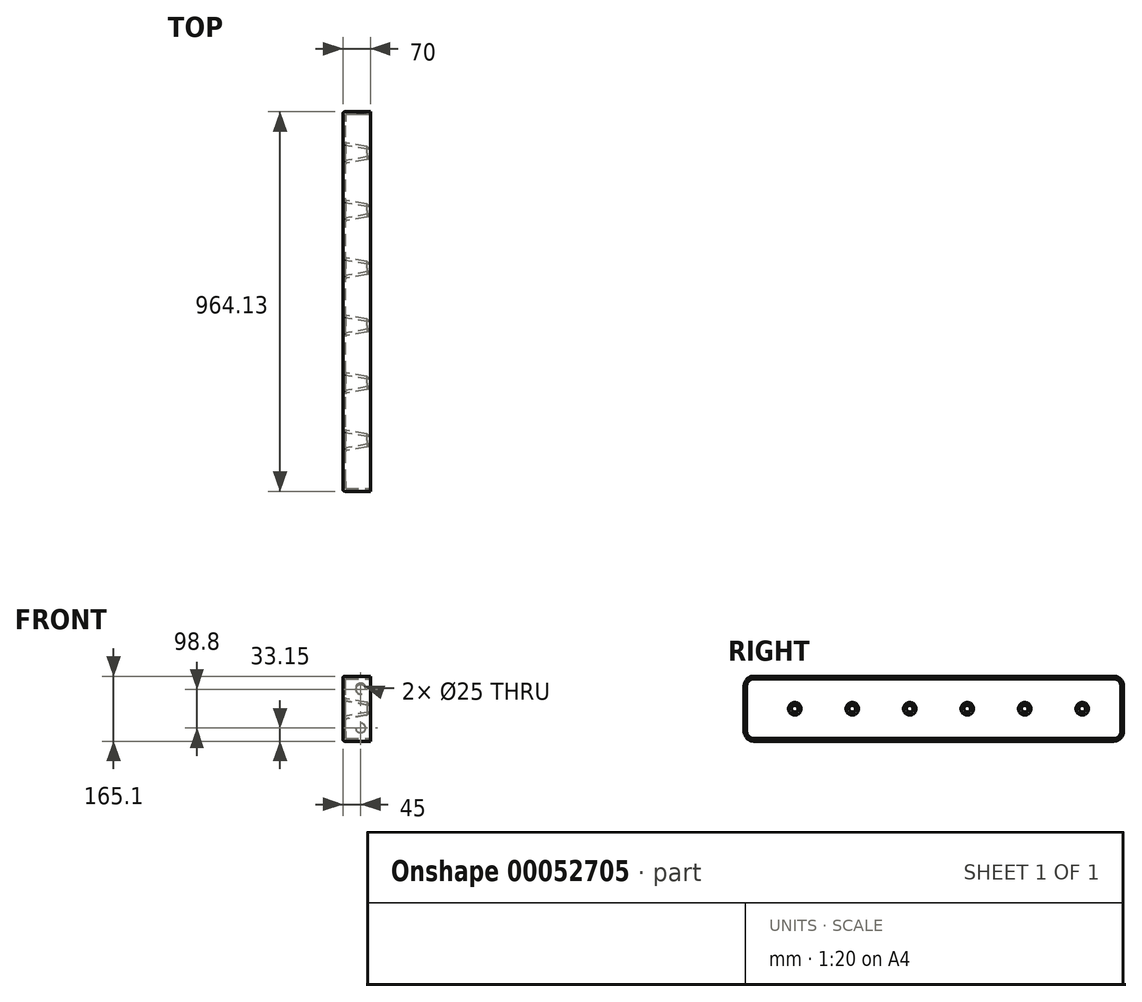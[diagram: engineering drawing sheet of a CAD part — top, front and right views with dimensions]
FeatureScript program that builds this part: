
annotation { "Feature Type Name" : "Feature", "Feature Type Description" : "" }
export const myFeature = defineFeature(function(context is Context, id is Id, definition is map)
    precondition{}
    {
        {
            var Q0;
            Q0=qCreatedBy(makeId("Right.planeOp"),FACE);
            var sketch = newSketch(context, id + "F0", { "sketchPlane" : qUnion([Q0])});
            skLineSegment(sketch, "E0.rect.bottom", {"start": v(-457.5, 82.55) * mm, "end": v(457.5, 82.55) * mm});
            skLineSegment(sketch, "E0.rect.top", {"start": v(-457.5, -82.55) * mm, "end": v(457.5, -82.55) * mm});
            skLineSegment(sketch, "E0.rect.left", {"start": v(-457.5, 82.55) * mm, "end": v(-457.5, -82.55) * mm});
            skLineSegment(sketch, "E0.rect.right", {"start": v(457.5, 82.55) * mm, "end": v(457.5, -82.55) * mm});
            skPoint(sketch, "E0.rect.middle", {"position": v(0, 0) * mm});
            skLineSegment(sketch, "E1.0", {"start": v(-447.34, 72.39) * mm, "end": v(447.34, 72.39) * mm, "construction": true});
            skLineSegment(sketch, "E1.1", {"start": v(-447.34, 72.39) * mm, "end": v(-447.34, -72.39) * mm, "construction": true});
            skLineSegment(sketch, "E1.2", {"start": v(-447.34, -72.39) * mm, "end": v(447.34, -72.39) * mm, "construction": true});
            skLineSegment(sketch, "E1.3", {"start": v(447.34, 72.39) * mm, "end": v(447.34, -72.39) * mm, "construction": true});
            skLineSegment(sketch, "E2", {"start": v(-457.5, 82.55) * mm, "end": v(457.5, -82.55) * mm, "construction": true});
            skLineSegment(sketch, "E3", {"start": v(457.5, 82.55) * mm, "end": v(-457.5, -82.55) * mm, "construction": true});
            skSolve(sketch);
        }
        {
            var Q0;
            Q0=makeQuery(id+"F0.imprint","IMPRINT",FACE,{"disambiguationData":[TD([[makeQuery(id+"F0.imprint","IMPRINT",EDGE,{"derivedFrom":sQuery(id+"F0.wireOp",EDGE,"E0.rect.bottom")}),-1.0]])]});
            extrude(context, id + "F1", {"entities" : qUnion([Q0]), "depth" : 70 * mm});
        }
        {
            var Q0;
            Q0=makeQuery(id+"F1.opExtrude","SWEPT_FACE",FACE,{"disambiguationData":[OSD([sQuery(id+"F0.wireOp",EDGE,"E0.rect.left")])]});
            extrude(context, id + "F2", {"entities" : qUnion([Q0]), "operationType" : NewBodyOperationType.ADD, "depth" : 36.63 * mm});
        }
        {
            var Q0;
            Q0=makeQuery(id+"F1.opExtrude","SWEPT_FACE",FACE,{"disambiguationData":[OSD([sQuery(id+"F0.wireOp",EDGE,"E0.rect.right")])]});
            extrude(context, id + "F3", {"entities" : qUnion([Q0]), "operationType" : NewBodyOperationType.ADD, "depth" : 12.5 * mm});
        }
        {
            var Q0;
            Q0=makeQuery(id+"F0.imprint","IMPRINT",FACE,{"disambiguationData":[TD([[makeQuery(id+"F0.imprint","IMPRINT",EDGE,{"derivedFrom":sQuery(id+"F0.wireOp",EDGE,"E0.rect.bottom")}),-1.0]])]});
            var sketch = newSketch(context, id + "F4", { "sketchPlane" : qUnion([Q0])});
            skLineSegment(sketch, "E4", {"start": v(-457.5, 0) * mm, "end": v(457.5, 0) * mm, "construction": true});
            skCircle(sketch, "E5", {"center": v(-365.13, 0) * mm, "radius": 20.32 * mm});
            skCircle(sketch, "E6", {"center": v(-73.03, 0) * mm, "radius": 20.32 * mm});
            skCircle(sketch, "E7.MirrorC", {"center": v(73.03, 0) * mm, "radius": 20.32 * mm});
            skCircle(sketch, "E8", {"center": v(-219.08, 0) * mm, "radius": 20.32 * mm});
            skCircle(sketch, "E9", {"center": v(219.08, 0) * mm, "radius": 20.32 * mm});
            skCircle(sketch, "E10", {"center": v(365.13, 0) * mm, "radius": 20.32 * mm});
            skSolve(sketch);
        }
        {
            var Q0;
            Q0 = qSketchRegion(id + "F4", true);
            extrude(context, id + "F5", {"entities" : qUnion([Q0]), "operationType" : NewBodyOperationType.REMOVE, "endBound" : BoundingType.THROUGH_ALL, "depth" : 25 * mm, "hasDraft" : true, "draftAngle" : 10 * degree, "draftPullDirection" : true});
        }
        {
            var Q0;
            {var subQ0=makeQuery(id+"FMJtkyeOeprAO9Q_1.hole-4.opRevolve","SWEPT_FACE",FACE,{"disambiguationData":[OSD([sQuery(id+"FMJtkyeOeprAO9Q_1.hole-4.sketch.wireOp",EDGE,"cbore_start_line_2")])]});var subQ1=makeQuery(id+"FMJtkyeOeprAO9Q_1.hole-2.boolean.opBoolean","COPY",FACE,{"derivedFrom":makeQuery(id+"FMJtkyeOeprAO9Q_1.hole-2.opRevolve","SWEPT_FACE",FACE,{"disambiguationData":[OSD([sQuery(id+"FMJtkyeOeprAO9Q_1.hole-2.sketch.wireOp",EDGE,"cbore_start_line_2")])]})});var subQ2=sQuery(id+"F0.wireOp",EDGE,"E0.rect.top");var subQ3=makeQuery(id+"F1.opExtrude","SWEPT_FACE",FACE,{"disambiguationData":[OSD([subQ2])]});var subQ4=makeQuery(id+"FMJtkyeOeprAO9Q_1.hole-3.opRevolve","SWEPT_FACE",FACE,{"disambiguationData":[OSD([sQuery(id+"FMJtkyeOeprAO9Q_1.hole-3.sketch.wireOp",EDGE,"cbore_start_line_2")])]});var subQ5=makeQuery(id+"FMJtkyeOeprAO9Q_1.hole-3.boolean.opBoolean","COPY",FACE,{"disambiguationData":[OD(1.0)],"derivedFrom":subQ4});var subQ6=makeQuery(id+"FMJtkyeOeprAO9Q_1.hole-0.opRevolve","SWEPT_FACE",FACE,{"disambiguationData":[OSD([sQuery(id+"FMJtkyeOeprAO9Q_1.hole-0.sketch.wireOp",EDGE,"cbore_start_line_2")])]});var subQ7=makeQuery(id+"FMJtkyeOeprAO9Q_1.hole-0.boolean.opBoolean","COPY",FACE,{"disambiguationData":[OD(1.0)],"derivedFrom":subQ6});var subQ8=makeQuery(id+"FMJtkyeOeprAO9Q_1.hole-1.boolean.opBoolean","COPY",FACE,{"derivedFrom":makeQuery(id+"FMJtkyeOeprAO9Q_1.hole-1.opRevolve","SWEPT_FACE",FACE,{"disambiguationData":[OSD([sQuery(id+"FMJtkyeOeprAO9Q_1.hole-1.sketch.wireOp",EDGE,"cbore_start_line_2")])]})});var subQ9=sQuery(id+"F0.wireOp",EDGE,"E0.rect.bottom");var subQ10=makeQuery(id+"F1.opExtrude","SWEPT_FACE",FACE,{"disambiguationData":[OSD([subQ9])]});var subQ11=sQuery(id+"F0.wireOp",EDGE,"E0.rect.left");var subQ12=makeQuery(id+"F1.opExtrude","SWEPT_FACE",FACE,{"disambiguationData":[OSD([subQ11])]});var subQ13=sQuery(id+"F0.wireOp",EDGE,"E0.rect.right");var subQ14=makeQuery(id+"F1.opExtrude","SWEPT_FACE",FACE,{"disambiguationData":[OSD([subQ13])]});Q0=makeQuery(id+"FMJtkyeOeprAO9Q_1.hole-7.boolean.opBoolean","SPLIT",FACE,{"disambiguationData":[TD([subQ10,subQ3,subQ12,subQ14,subQ7,subQ8,subQ1,subQ5,makeQuery(id+"FMJtkyeOeprAO9Q_1.hole-4.boolean.opBoolean","COPY",FACE,{"disambiguationData":[OD(1.0)],"derivedFrom":subQ0}),makeQuery(id+"FMJtkyeOeprAO9Q_1.hole-5.boolean.opBoolean","COPY",FACE,{"derivedFrom":makeQuery(id+"FMJtkyeOeprAO9Q_1.hole-5.opRevolve","SWEPT_FACE",FACE,{"disambiguationData":[OSD([sQuery(id+"FMJtkyeOeprAO9Q_1.hole-5.sketch.wireOp",EDGE,"cbore_start_line_2")])]})}),makeQuery(id+"FMJtkyeOeprAO9Q_1.hole-6.boolean.opBoolean","COPY",FACE,{"derivedFrom":makeQuery(id+"FMJtkyeOeprAO9Q_1.hole-6.opRevolve","SWEPT_FACE",FACE,{"disambiguationData":[OSD([sQuery(id+"FMJtkyeOeprAO9Q_1.hole-6.sketch.wireOp",EDGE,"cbore_start_line_2")])]})}),makeQuery(id+"FMJtkyeOeprAO9Q_1.hole-7.opRevolve","SWEPT_FACE",FACE,{"disambiguationData":[OSD([sQuery(id+"FMJtkyeOeprAO9Q_1.hole-7.sketch.wireOp",EDGE,"cbore_start_line_2")])]})])],"derivedFrom":makeQuery(id+"FMJtkyeOeprAO9Q_1.hole-4.boolean.opBoolean","SPLIT",FACE,{"disambiguationData":[TD([subQ10,subQ3,subQ12,subQ14,subQ7,subQ8,subQ1,subQ5,subQ0])],"derivedFrom":makeQuery(id+"FMJtkyeOeprAO9Q_1.hole-3.boolean.opBoolean","SPLIT",FACE,{"disambiguationData":[TD([subQ10,subQ3,subQ12,subQ14,subQ7,subQ8,subQ1,subQ4])],"derivedFrom":makeQuery(id+"FMJtkyeOeprAO9Q_1.hole-0.boolean.opBoolean","SPLIT",FACE,{"disambiguationData":[TD([subQ10,subQ3,subQ12,subQ14,subQ6])],"derivedFrom":makeQuery(id+"F1.opExtrude","CAP_FACE",FACE,{"disambiguationData":[OSD([subQ9,subQ2,subQ11,subQ13])],"isStart":true})})})})});}
            fillet(context, id + "F6", {"entities" : qUnion([Q0]), "radius" : 5 * mm, "tangentPropagation" : true, "allowEdgeOverflow" : false});
        }
        {
            var Q0;
            Q0=makeQuery(id+"F2.opExtrude","CAP_EDGE",EDGE,{"disambiguationData":[OSD([sQuery(id+"F0.wireOp",EDGE,"E0.rect.bottom"),sQuery(id+"F0.wireOp",EDGE,"E0.rect.left")])],"isStart":false});
            var Q1;
            Q1=makeQuery(id+"F2.opExtrude","CAP_EDGE",EDGE,{"disambiguationData":[OSD([sQuery(id+"F0.wireOp",EDGE,"E0.rect.top"),sQuery(id+"F0.wireOp",EDGE,"E0.rect.left")])],"isStart":false});
            var Q2;
            Q2=makeQuery(id+"F3.opExtrude","CAP_EDGE",EDGE,{"disambiguationData":[OSD([sQuery(id+"F0.wireOp",EDGE,"E0.rect.top"),sQuery(id+"F0.wireOp",EDGE,"E0.rect.right")])],"isStart":false});
            var Q3;
            Q3=makeQuery(id+"F3.opExtrude","CAP_EDGE",EDGE,{"disambiguationData":[OSD([sQuery(id+"F0.wireOp",EDGE,"E0.rect.bottom"),sQuery(id+"F0.wireOp",EDGE,"E0.rect.right")])],"isStart":false});
            fillet(context, id + "F7", {"entities" : qUnion([Q0, Q1, Q2, Q3]), "radius" : 25.4 * mm, "tangentPropagation" : true, "allowEdgeOverflow" : false});
        }
        {
            var Q0;
            Q0=makeQuery(id+"F1.opExtrude","CAP_FACE",FACE,{"disambiguationData":[OSD([sQuery(id+"F0.wireOp",EDGE,"E0.rect.bottom"),sQuery(id+"F0.wireOp",EDGE,"E0.rect.top"),sQuery(id+"F0.wireOp",EDGE,"E0.rect.left"),sQuery(id+"F0.wireOp",EDGE,"E0.rect.right")])],"isStart":false});
            shell(context, id + "F8", {"entities" : qUnion([Q0]), "thickness" : 6.5 * mm});
        }
        {
            var Q0;
            {var subQ0=makeQuery(id+"FMJtkyeOeprAO9Q_1.hole-4.opRevolve","SWEPT_FACE",FACE,{"disambiguationData":[OSD([sQuery(id+"FMJtkyeOeprAO9Q_1.hole-4.sketch.wireOp",EDGE,"cbore_start_line_2")])]});var subQ1=makeQuery(id+"FMJtkyeOeprAO9Q_1.hole-2.boolean.opBoolean","COPY",FACE,{"derivedFrom":makeQuery(id+"FMJtkyeOeprAO9Q_1.hole-2.opRevolve","SWEPT_FACE",FACE,{"disambiguationData":[OSD([sQuery(id+"FMJtkyeOeprAO9Q_1.hole-2.sketch.wireOp",EDGE,"cbore_start_line_2")])]})});var subQ2=sQuery(id+"F0.wireOp",EDGE,"E0.rect.top");var subQ3=makeQuery(id+"F1.opExtrude","SWEPT_FACE",FACE,{"disambiguationData":[OSD([subQ2])]});var subQ4=makeQuery(id+"FMJtkyeOeprAO9Q_1.hole-3.opRevolve","SWEPT_FACE",FACE,{"disambiguationData":[OSD([sQuery(id+"FMJtkyeOeprAO9Q_1.hole-3.sketch.wireOp",EDGE,"cbore_start_line_2")])]});var subQ5=makeQuery(id+"FMJtkyeOeprAO9Q_1.hole-3.boolean.opBoolean","COPY",FACE,{"disambiguationData":[OD(1.0)],"derivedFrom":subQ4});var subQ6=makeQuery(id+"FMJtkyeOeprAO9Q_1.hole-0.opRevolve","SWEPT_FACE",FACE,{"disambiguationData":[OSD([sQuery(id+"FMJtkyeOeprAO9Q_1.hole-0.sketch.wireOp",EDGE,"cbore_start_line_2")])]});var subQ7=makeQuery(id+"FMJtkyeOeprAO9Q_1.hole-0.boolean.opBoolean","COPY",FACE,{"disambiguationData":[OD(1.0)],"derivedFrom":subQ6});var subQ8=makeQuery(id+"FMJtkyeOeprAO9Q_1.hole-1.boolean.opBoolean","COPY",FACE,{"derivedFrom":makeQuery(id+"FMJtkyeOeprAO9Q_1.hole-1.opRevolve","SWEPT_FACE",FACE,{"disambiguationData":[OSD([sQuery(id+"FMJtkyeOeprAO9Q_1.hole-1.sketch.wireOp",EDGE,"cbore_start_line_2")])]})});var subQ9=sQuery(id+"F0.wireOp",EDGE,"E0.rect.bottom");var subQ10=makeQuery(id+"F1.opExtrude","SWEPT_FACE",FACE,{"disambiguationData":[OSD([subQ9])]});var subQ11=sQuery(id+"F0.wireOp",EDGE,"E0.rect.left");var subQ12=makeQuery(id+"F1.opExtrude","SWEPT_FACE",FACE,{"disambiguationData":[OSD([subQ11])]});var subQ13=sQuery(id+"F0.wireOp",EDGE,"E0.rect.right");var subQ14=makeQuery(id+"F1.opExtrude","SWEPT_FACE",FACE,{"disambiguationData":[OSD([subQ13])]});Q0=makeQuery(id+"F8.opShell","OFFSET_FACE",FACE,{"disambiguationData":[OSD([subQ9,subQ2,subQ11,subQ13]),TDD([makeQuery(id+"FMJtkyeOeprAO9Q_1.hole-7.boolean.opBoolean","SPLIT",FACE,{"disambiguationData":[TD([subQ10,subQ3,subQ12,subQ14,subQ7,subQ8,subQ1,subQ5,makeQuery(id+"FMJtkyeOeprAO9Q_1.hole-4.boolean.opBoolean","COPY",FACE,{"disambiguationData":[OD(1.0)],"derivedFrom":subQ0}),makeQuery(id+"FMJtkyeOeprAO9Q_1.hole-5.boolean.opBoolean","COPY",FACE,{"derivedFrom":makeQuery(id+"FMJtkyeOeprAO9Q_1.hole-5.opRevolve","SWEPT_FACE",FACE,{"disambiguationData":[OSD([sQuery(id+"FMJtkyeOeprAO9Q_1.hole-5.sketch.wireOp",EDGE,"cbore_start_line_2")])]})}),makeQuery(id+"FMJtkyeOeprAO9Q_1.hole-6.boolean.opBoolean","COPY",FACE,{"derivedFrom":makeQuery(id+"FMJtkyeOeprAO9Q_1.hole-6.opRevolve","SWEPT_FACE",FACE,{"disambiguationData":[OSD([sQuery(id+"FMJtkyeOeprAO9Q_1.hole-6.sketch.wireOp",EDGE,"cbore_start_line_2")])]})}),makeQuery(id+"FMJtkyeOeprAO9Q_1.hole-7.opRevolve","SWEPT_FACE",FACE,{"disambiguationData":[OSD([sQuery(id+"FMJtkyeOeprAO9Q_1.hole-7.sketch.wireOp",EDGE,"cbore_start_line_2")])]})])],"derivedFrom":makeQuery(id+"FMJtkyeOeprAO9Q_1.hole-4.boolean.opBoolean","SPLIT",FACE,{"disambiguationData":[TD([subQ10,subQ3,subQ12,subQ14,subQ7,subQ8,subQ1,subQ5,subQ0])],"derivedFrom":makeQuery(id+"FMJtkyeOeprAO9Q_1.hole-3.boolean.opBoolean","SPLIT",FACE,{"disambiguationData":[TD([subQ10,subQ3,subQ12,subQ14,subQ7,subQ8,subQ1,subQ4])],"derivedFrom":makeQuery(id+"FMJtkyeOeprAO9Q_1.hole-0.boolean.opBoolean","SPLIT",FACE,{"disambiguationData":[TD([subQ10,subQ3,subQ12,subQ14,subQ6])],"derivedFrom":makeQuery(id+"F1.opExtrude","CAP_FACE",FACE,{"disambiguationData":[OSD([subQ9,subQ2,subQ11,subQ13])],"isStart":true})})})})})])]});}
            fillet(context, id + "F9", {"entities" : qUnion([Q0]), "radius" : 3.17 * mm, "tangentPropagation" : true, "allowEdgeOverflow" : false});
        }
        {
            var Q0;
            {var subQ0=sQuery(id+"F4.wireOp",EDGE,"E5");var subQ1=sQuery(id+"F0.wireOp",EDGE,"E0.rect.right");var subQ2=sQuery(id+"F0.wireOp",EDGE,"E0.rect.left");var subQ3=sQuery(id+"F0.wireOp",EDGE,"E0.rect.top");var subQ4=sQuery(id+"F0.wireOp",EDGE,"E0.rect.bottom");Q0=makeQuery(id+"F8.opShell","OFFSET_EDGE",EDGE,{"disambiguationData":[OSD([subQ4,subQ3,subQ2,subQ1,subQ0]),TDD([makeQuery(id+"F5.boolean.opBoolean","INTERSECT",EDGE,{"derivedFrom":[makeQuery(id+"F3.boolean.opBoolean","MERGE",FACE,{"derivedFrom":[makeQuery(id+"F2.boolean.opBoolean","MERGE",FACE,{"derivedFrom":[makeQuery(id+"F1.opExtrude","CAP_FACE",FACE,{"disambiguationData":[OSD([subQ4,subQ3,subQ2,subQ1])],"isStart":false}),makeQuery(id+"F2.opExtrude","SWEPT_FACE",FACE,{"disambiguationData":[OSD([subQ2]),TDD([makeQuery(id+"F1.opExtrude","CAP_EDGE",EDGE,{"disambiguationData":[OSD([subQ2])],"isStart":false})])]})]}),makeQuery(id+"F3.opExtrude","SWEPT_FACE",FACE,{"disambiguationData":[OSD([subQ1]),TDD([makeQuery(id+"F1.opExtrude","CAP_EDGE",EDGE,{"disambiguationData":[OSD([subQ1])],"isStart":false})])]})]}),makeQuery(id+"F5.opExtrude","SWEPT_FACE",FACE,{"disambiguationData":[OSD([subQ0])]})]})])]});}
            var Q1;
            {var subQ0=sQuery(id+"F4.wireOp",EDGE,"E8");var subQ1=sQuery(id+"F0.wireOp",EDGE,"E0.rect.right");var subQ2=sQuery(id+"F0.wireOp",EDGE,"E0.rect.left");var subQ3=sQuery(id+"F0.wireOp",EDGE,"E0.rect.top");var subQ4=sQuery(id+"F0.wireOp",EDGE,"E0.rect.bottom");Q1=makeQuery(id+"F8.opShell","OFFSET_EDGE",EDGE,{"disambiguationData":[OSD([subQ4,subQ3,subQ2,subQ1,subQ0]),TDD([makeQuery(id+"F5.boolean.opBoolean","INTERSECT",EDGE,{"derivedFrom":[makeQuery(id+"F3.boolean.opBoolean","MERGE",FACE,{"derivedFrom":[makeQuery(id+"F2.boolean.opBoolean","MERGE",FACE,{"derivedFrom":[makeQuery(id+"F1.opExtrude","CAP_FACE",FACE,{"disambiguationData":[OSD([subQ4,subQ3,subQ2,subQ1])],"isStart":false}),makeQuery(id+"F2.opExtrude","SWEPT_FACE",FACE,{"disambiguationData":[OSD([subQ2]),TDD([makeQuery(id+"F1.opExtrude","CAP_EDGE",EDGE,{"disambiguationData":[OSD([subQ2])],"isStart":false})])]})]}),makeQuery(id+"F3.opExtrude","SWEPT_FACE",FACE,{"disambiguationData":[OSD([subQ1]),TDD([makeQuery(id+"F1.opExtrude","CAP_EDGE",EDGE,{"disambiguationData":[OSD([subQ1])],"isStart":false})])]})]}),makeQuery(id+"F5.opExtrude","SWEPT_FACE",FACE,{"disambiguationData":[OSD([subQ0])]})]})])]});}
            var Q2;
            {var subQ0=sQuery(id+"F4.wireOp",EDGE,"E6");var subQ1=sQuery(id+"F0.wireOp",EDGE,"E0.rect.right");var subQ2=sQuery(id+"F0.wireOp",EDGE,"E0.rect.left");var subQ3=sQuery(id+"F0.wireOp",EDGE,"E0.rect.top");var subQ4=sQuery(id+"F0.wireOp",EDGE,"E0.rect.bottom");Q2=makeQuery(id+"F8.opShell","OFFSET_EDGE",EDGE,{"disambiguationData":[OSD([subQ4,subQ3,subQ2,subQ1,subQ0]),TDD([makeQuery(id+"F5.boolean.opBoolean","INTERSECT",EDGE,{"derivedFrom":[makeQuery(id+"F3.boolean.opBoolean","MERGE",FACE,{"derivedFrom":[makeQuery(id+"F2.boolean.opBoolean","MERGE",FACE,{"derivedFrom":[makeQuery(id+"F1.opExtrude","CAP_FACE",FACE,{"disambiguationData":[OSD([subQ4,subQ3,subQ2,subQ1])],"isStart":false}),makeQuery(id+"F2.opExtrude","SWEPT_FACE",FACE,{"disambiguationData":[OSD([subQ2]),TDD([makeQuery(id+"F1.opExtrude","CAP_EDGE",EDGE,{"disambiguationData":[OSD([subQ2])],"isStart":false})])]})]}),makeQuery(id+"F3.opExtrude","SWEPT_FACE",FACE,{"disambiguationData":[OSD([subQ1]),TDD([makeQuery(id+"F1.opExtrude","CAP_EDGE",EDGE,{"disambiguationData":[OSD([subQ1])],"isStart":false})])]})]}),makeQuery(id+"F5.opExtrude","SWEPT_FACE",FACE,{"disambiguationData":[OSD([subQ0])]})]})])]});}
            var Q3;
            {var subQ0=sQuery(id+"F4.wireOp",EDGE,"E7.MirrorC");var subQ1=sQuery(id+"F0.wireOp",EDGE,"E0.rect.right");var subQ2=sQuery(id+"F0.wireOp",EDGE,"E0.rect.left");var subQ3=sQuery(id+"F0.wireOp",EDGE,"E0.rect.top");var subQ4=sQuery(id+"F0.wireOp",EDGE,"E0.rect.bottom");Q3=makeQuery(id+"F8.opShell","OFFSET_EDGE",EDGE,{"disambiguationData":[OSD([subQ4,subQ3,subQ2,subQ1,subQ0]),TDD([makeQuery(id+"F5.boolean.opBoolean","INTERSECT",EDGE,{"derivedFrom":[makeQuery(id+"F3.boolean.opBoolean","MERGE",FACE,{"derivedFrom":[makeQuery(id+"F2.boolean.opBoolean","MERGE",FACE,{"derivedFrom":[makeQuery(id+"F1.opExtrude","CAP_FACE",FACE,{"disambiguationData":[OSD([subQ4,subQ3,subQ2,subQ1])],"isStart":false}),makeQuery(id+"F2.opExtrude","SWEPT_FACE",FACE,{"disambiguationData":[OSD([subQ2]),TDD([makeQuery(id+"F1.opExtrude","CAP_EDGE",EDGE,{"disambiguationData":[OSD([subQ2])],"isStart":false})])]})]}),makeQuery(id+"F3.opExtrude","SWEPT_FACE",FACE,{"disambiguationData":[OSD([subQ1]),TDD([makeQuery(id+"F1.opExtrude","CAP_EDGE",EDGE,{"disambiguationData":[OSD([subQ1])],"isStart":false})])]})]}),makeQuery(id+"F5.opExtrude","SWEPT_FACE",FACE,{"disambiguationData":[OSD([subQ0])]})]})])]});}
            var Q4;
            {var subQ0=sQuery(id+"F4.wireOp",EDGE,"E9");var subQ1=sQuery(id+"F0.wireOp",EDGE,"E0.rect.right");var subQ2=sQuery(id+"F0.wireOp",EDGE,"E0.rect.left");var subQ3=sQuery(id+"F0.wireOp",EDGE,"E0.rect.top");var subQ4=sQuery(id+"F0.wireOp",EDGE,"E0.rect.bottom");Q4=makeQuery(id+"F8.opShell","OFFSET_EDGE",EDGE,{"disambiguationData":[OSD([subQ4,subQ3,subQ2,subQ1,subQ0]),TDD([makeQuery(id+"F5.boolean.opBoolean","INTERSECT",EDGE,{"derivedFrom":[makeQuery(id+"F3.boolean.opBoolean","MERGE",FACE,{"derivedFrom":[makeQuery(id+"F2.boolean.opBoolean","MERGE",FACE,{"derivedFrom":[makeQuery(id+"F1.opExtrude","CAP_FACE",FACE,{"disambiguationData":[OSD([subQ4,subQ3,subQ2,subQ1])],"isStart":false}),makeQuery(id+"F2.opExtrude","SWEPT_FACE",FACE,{"disambiguationData":[OSD([subQ2]),TDD([makeQuery(id+"F1.opExtrude","CAP_EDGE",EDGE,{"disambiguationData":[OSD([subQ2])],"isStart":false})])]})]}),makeQuery(id+"F3.opExtrude","SWEPT_FACE",FACE,{"disambiguationData":[OSD([subQ1]),TDD([makeQuery(id+"F1.opExtrude","CAP_EDGE",EDGE,{"disambiguationData":[OSD([subQ1])],"isStart":false})])]})]}),makeQuery(id+"F5.opExtrude","SWEPT_FACE",FACE,{"disambiguationData":[OSD([subQ0])]})]})])]});}
            var Q5;
            {var subQ0=sQuery(id+"F4.wireOp",EDGE,"E10");var subQ1=sQuery(id+"F0.wireOp",EDGE,"E0.rect.right");var subQ2=sQuery(id+"F0.wireOp",EDGE,"E0.rect.left");var subQ3=sQuery(id+"F0.wireOp",EDGE,"E0.rect.top");var subQ4=sQuery(id+"F0.wireOp",EDGE,"E0.rect.bottom");Q5=makeQuery(id+"F8.opShell","OFFSET_EDGE",EDGE,{"disambiguationData":[OSD([subQ4,subQ3,subQ2,subQ1,subQ0]),TDD([makeQuery(id+"F5.boolean.opBoolean","INTERSECT",EDGE,{"derivedFrom":[makeQuery(id+"F3.boolean.opBoolean","MERGE",FACE,{"derivedFrom":[makeQuery(id+"F2.boolean.opBoolean","MERGE",FACE,{"derivedFrom":[makeQuery(id+"F1.opExtrude","CAP_FACE",FACE,{"disambiguationData":[OSD([subQ4,subQ3,subQ2,subQ1])],"isStart":false}),makeQuery(id+"F2.opExtrude","SWEPT_FACE",FACE,{"disambiguationData":[OSD([subQ2]),TDD([makeQuery(id+"F1.opExtrude","CAP_EDGE",EDGE,{"disambiguationData":[OSD([subQ2])],"isStart":false})])]})]}),makeQuery(id+"F3.opExtrude","SWEPT_FACE",FACE,{"disambiguationData":[OSD([subQ1]),TDD([makeQuery(id+"F1.opExtrude","CAP_EDGE",EDGE,{"disambiguationData":[OSD([subQ1])],"isStart":false})])]})]}),makeQuery(id+"F5.opExtrude","SWEPT_FACE",FACE,{"disambiguationData":[OSD([subQ0])]})]})])]});}
            chamfer(context, id + "F10", {"entities" : qUnion([Q0, Q1, Q2, Q3, Q4, Q5]), "width" : 10 * mm, "tangentPropagation" : true});
        }
        {
            var Q0;
            Q0=makeQuery(id+"F3.opExtrude","CAP_FACE",FACE,{"disambiguationData":[OSD([sQuery(id+"F0.wireOp",EDGE,"E0.rect.right")])],"isStart":false});
            var sketch = newSketch(context, id + "F11", { "sketchPlane" : qUnion([Q0])});
            skCircle(sketch, "E11", {"center": v(-45, 49.4) * mm, "radius": 12.5 * mm});
            skCircle(sketch, "E12", {"center": v(-45, -49.4) * mm, "radius": 12.5 * mm});
            skSolve(sketch);
        }
        {
            var Q0;
            {var subQ0=sQuery(id+"F11.wireOp",EDGE,"E11");var subQ1=sQuery(id+"F0.wireOp",EDGE,"E0.rect.right");var subQ2=makeQuery(id+"F7.opFillet","BLEND_EDGE",EDGE,{"blendedFrom":[makeQuery(id+"F3.opExtrude","CAP_EDGE",EDGE,{"disambiguationData":[OSD([sQuery(id+"F0.wireOp",EDGE,"E0.rect.bottom"),subQ1])],"isStart":false}),makeQuery(id+"F3.opExtrude","CAP_FACE",FACE,{"disambiguationData":[OSD([subQ1])],"isStart":false})],"blendedInto":[makeQuery(id+"F3.opExtrude","CAP_FACE",FACE,{"disambiguationData":[OSD([subQ1])],"isStart":false})]});var subQ3=makeQuery(id+"F11.imprint","INTERSECT",VERTEX,{"disambiguationData":[OD(0.0)],"derivedFrom":[subQ2,subQ0]});Q0=makeQuery(id+"F11.imprint","IMPRINT",FACE,{"disambiguationData":[TD([[makeQuery(id+"F11.imprint","IMPRINT",EDGE,{"disambiguationData":[TD([[subQ3,-1.0]])],"derivedFrom":subQ0}),1.0]])]});}
            var Q1;
            {var subQ0=sQuery(id+"F11.wireOp",EDGE,"E11");var subQ1=sQuery(id+"F0.wireOp",EDGE,"E0.rect.right");var subQ2=makeQuery(id+"F7.opFillet","BLEND_EDGE",EDGE,{"blendedFrom":[makeQuery(id+"F3.opExtrude","CAP_EDGE",EDGE,{"disambiguationData":[OSD([sQuery(id+"F0.wireOp",EDGE,"E0.rect.bottom"),subQ1])],"isStart":false}),makeQuery(id+"F3.opExtrude","CAP_FACE",FACE,{"disambiguationData":[OSD([subQ1])],"isStart":false})],"blendedInto":[makeQuery(id+"F3.opExtrude","CAP_FACE",FACE,{"disambiguationData":[OSD([subQ1])],"isStart":false})]});var subQ3=makeQuery(id+"F11.imprint","INTERSECT",VERTEX,{"disambiguationData":[OD(0.0)],"derivedFrom":[subQ2,subQ0]});Q1=makeQuery(id+"F11.imprint","IMPRINT",FACE,{"disambiguationData":[TD([[makeQuery(id+"F11.imprint","IMPRINT",EDGE,{"disambiguationData":[TD([[subQ3,1.0]])],"derivedFrom":subQ0}),1.0]])]});}
            var Q2;
            {var subQ0=sQuery(id+"F11.wireOp",EDGE,"E12");var subQ1=sQuery(id+"F0.wireOp",EDGE,"E0.rect.right");var subQ2=makeQuery(id+"F7.opFillet","BLEND_EDGE",EDGE,{"blendedFrom":[makeQuery(id+"F3.opExtrude","CAP_EDGE",EDGE,{"disambiguationData":[OSD([sQuery(id+"F0.wireOp",EDGE,"E0.rect.top"),subQ1])],"isStart":false}),makeQuery(id+"F3.opExtrude","CAP_FACE",FACE,{"disambiguationData":[OSD([subQ1])],"isStart":false})],"blendedInto":[makeQuery(id+"F3.opExtrude","CAP_FACE",FACE,{"disambiguationData":[OSD([subQ1])],"isStart":false})]});var subQ3=makeQuery(id+"F11.imprint","INTERSECT",VERTEX,{"disambiguationData":[OD(0.0)],"derivedFrom":[subQ2,subQ0]});Q2=makeQuery(id+"F11.imprint","IMPRINT",FACE,{"disambiguationData":[TD([[makeQuery(id+"F11.imprint","IMPRINT",EDGE,{"disambiguationData":[TD([[subQ3,1.0]])],"derivedFrom":subQ0}),1.0]])]});}
            var Q3;
            {var subQ0=sQuery(id+"F11.wireOp",EDGE,"E12");var subQ1=sQuery(id+"F0.wireOp",EDGE,"E0.rect.right");var subQ2=makeQuery(id+"F7.opFillet","BLEND_EDGE",EDGE,{"blendedFrom":[makeQuery(id+"F3.opExtrude","CAP_EDGE",EDGE,{"disambiguationData":[OSD([sQuery(id+"F0.wireOp",EDGE,"E0.rect.top"),subQ1])],"isStart":false}),makeQuery(id+"F3.opExtrude","CAP_FACE",FACE,{"disambiguationData":[OSD([subQ1])],"isStart":false})],"blendedInto":[makeQuery(id+"F3.opExtrude","CAP_FACE",FACE,{"disambiguationData":[OSD([subQ1])],"isStart":false})]});var subQ3=makeQuery(id+"F11.imprint","INTERSECT",VERTEX,{"disambiguationData":[OD(0.0)],"derivedFrom":[subQ2,subQ0]});Q3=makeQuery(id+"F11.imprint","IMPRINT",FACE,{"disambiguationData":[TD([[makeQuery(id+"F11.imprint","IMPRINT",EDGE,{"disambiguationData":[TD([[subQ3,-1.0]])],"derivedFrom":subQ0}),1.0]])]});}
            extrude(context, id + "F12", {"entities" : qUnion([Q0, Q1, Q2, Q3]), "operationType" : NewBodyOperationType.REMOVE, "oppositeDirection" : true, "depth" : 25 * mm});
        }
        {
            var Q0;
            Q0=makeQuery(id+"F12.boolean.opBoolean","INTERSECT",EDGE,{"derivedFrom":[makeQuery(id+"F7.opFillet","BLEND_FACE",FACE,{"disambiguationData":[OSD([sQuery(id+"F0.wireOp",EDGE,"E0.rect.bottom"),sQuery(id+"F0.wireOp",EDGE,"E0.rect.right")])]}),makeQuery(id+"F12.opExtrude","SWEPT_FACE",FACE,{"disambiguationData":[OSD([sQuery(id+"F11.wireOp",EDGE,"E11")])]})]});
            var Q1;
            Q1=makeQuery(id+"F12.boolean.opBoolean","COPY",EDGE,{"derivedFrom":makeQuery(id+"F12.opExtrude","CAP_EDGE",EDGE,{"disambiguationData":[OSD([sQuery(id+"F11.wireOp",EDGE,"E11")])],"isStart":true})});
            var Q2;
            Q2=makeQuery(id+"F12.boolean.opBoolean","COPY",EDGE,{"derivedFrom":makeQuery(id+"F12.opExtrude","CAP_EDGE",EDGE,{"disambiguationData":[OSD([sQuery(id+"F11.wireOp",EDGE,"E12")])],"isStart":true})});
            fillet(context, id + "F13", {"entities" : qUnion([Q0, Q1, Q2]), "radius" : 2 * mm, "tangentPropagation" : true, "allowEdgeOverflow" : false});
        }
    });
